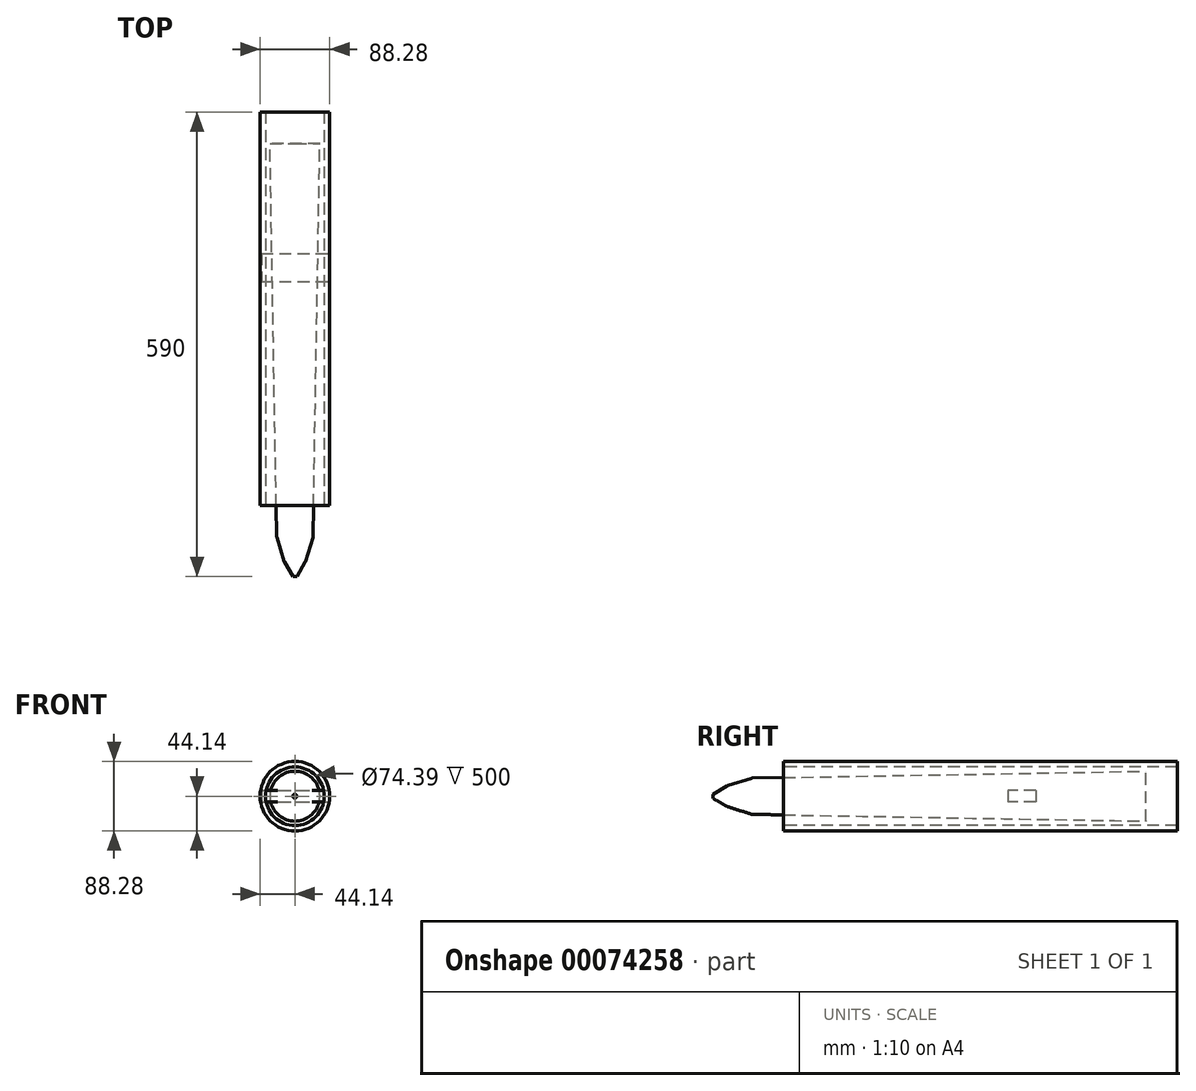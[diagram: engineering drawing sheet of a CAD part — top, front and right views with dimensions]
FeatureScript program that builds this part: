
annotation { "Feature Type Name" : "Feature", "Feature Type Description" : "" }
export const myFeature = defineFeature(function(context is Context, id is Id, definition is map)
    precondition{}
    {
        {
            var Q0;
            Q0=qCreatedBy(makeId("Front.planeOp"),FACE);
            var sketch = newSketch(context, id + "F0", { "sketchPlane" : qUnion([Q0])});
            skCircle(sketch, "E0", {"center": v(0, 0) * mm, "radius": 44.14 * mm});
            skSolve(sketch);
        }
        {
            var Q0;
            Q0=makeQuery(id+"F0.imprint","IMPRINT",FACE,{"disambiguationData":[TD([[makeQuery(id+"F0.imprint","IMPRINT",EDGE,{"derivedFrom":sQuery(id+"F0.wireOp",EDGE,"E0")}),1.0]])]});
            extrude(context, id + "F1", {"entities" : qUnion([Q0]), "endBound" : BoundingType.SYMMETRIC, "depth" : 500 * mm});
        }
        {
            var Q0;
            Q0=qCreatedBy(makeId("Front.planeOp"),FACE);
            var sketch = newSketch(context, id + "F2", { "sketchPlane" : qUnion([Q0])});
            skCircle(sketch, "E1", {"center": v(0, 0) * mm, "radius": 37.2 * mm});
            skSolve(sketch);
        }
        {
            var Q0;
            Q0=makeQuery(id+"F2.imprint","IMPRINT",FACE,{"disambiguationData":[TD([[makeQuery(id+"F2.imprint","IMPRINT",EDGE,{"derivedFrom":sQuery(id+"F2.wireOp",EDGE,"E1")}),1.0]])]});
            extrude(context, id + "F3", {"entities" : qUnion([Q0]), "operationType" : NewBodyOperationType.REMOVE, "endBound" : BoundingType.SYMMETRIC, "oppositeDirection" : true, "depth" : 550 * mm});
        }
        {
            var Q0;
            Q0=qCreatedBy(makeId("Front.planeOp"),FACE);
            cPlane(context, id + "F4", {"entities" : qUnion([Q0]), "cplaneType" : CPlaneType.OFFSET, "offset" : 290 * mm, "width" : 150 * mm, "height" : 150 * mm});
        }
        {
            var Q0;
            Q0=qCreatedBy(id+"F4.planeOp",FACE);
            var sketch = newSketch(context, id + "F5", { "sketchPlane" : qUnion([Q0])});
            skCircle(sketch, "E2", {"center": v(0, 0) * mm, "radius": 23.03 * mm});
            skSolve(sketch);
        }
        {
            var Q0;
            Q0=qCreatedBy(id+"F4.planeOp",FACE);
            cPlane(context, id + "F6", {"entities" : qUnion([Q0]), "cplaneType" : CPlaneType.OFFSET, "offset" : 500 * mm, "oppositeDirection" : true, "width" : 150 * mm, "height" : 150 * mm});
        }
        {
            var Q0;
            Q0=qCreatedBy(id+"F6.planeOp",FACE);
            var sketch = newSketch(context, id + "F7", { "sketchPlane" : qUnion([Q0])});
            skCircle(sketch, "E3", {"center": v(0, 0) * mm, "radius": 31.73 * mm});
            skSolve(sketch);
        }
        {
            var Q1;
            Q1 = qSketchRegion(id + "F7", true);
            var Q2;
            Q2 = qSketchRegion(id + "F5", true);
            loft(context, id + "F8", {"operationType" : NewBodyOperationType.ADD, "sheetProfilesArray" : [{ "sheetProfileEntities" : qUnion([Q1]) }, { "sheetProfileEntities" : qUnion([Q2]) }]});
        }
        {
            var Q0;
            Q0=qCreatedBy(makeId("Top.planeOp"),FACE);
            var sketch = newSketch(context, id + "F9", { "sketchPlane" : qUnion([Q0])});
            skLineSegment(sketch, "E4", {"start": v(0, 70.47) * mm, "end": v(-42.54, 70.47) * mm});
            skLineSegment(sketch, "E5", {"start": v(-42.54, 70.47) * mm, "end": v(-42.54, 34.9) * mm});
            skLineSegment(sketch, "E6", {"start": v(-42.54, 34.9) * mm, "end": v(0, 34.9) * mm});
            skLineSegment(sketch, "E7.MirrorCS", {"start": v(0, 70.47) * mm, "end": v(42.54, 70.47) * mm});
            skLineSegment(sketch, "E8.MirrorCS", {"start": v(42.54, 70.47) * mm, "end": v(42.54, 34.9) * mm});
            skLineSegment(sketch, "E9.MirrorCS", {"start": v(42.54, 34.9) * mm, "end": v(0, 34.9) * mm});
            skSolve(sketch);
        }
        {
            var Q0;
            Q0 = qSketchRegion(id + "F9", true);
            extrude(context, id + "F10", {"entities" : qUnion([Q0]), "endBound" : BoundingType.SYMMETRIC, "depth" : 15 * mm});
        }
        {
            var Q0;
            Q0=qCreatedBy(id+"F4.planeOp",FACE);
            cPlane(context, id + "F11", {"entities" : qUnion([Q0]), "cplaneType" : CPlaneType.OFFSET, "offset" : 50 * mm, "width" : 150 * mm, "height" : 150 * mm});
        }
        {
            var Q0;
            Q0=qCreatedBy(id+"F11.planeOp",FACE);
            var sketch = newSketch(context, id + "F12", { "sketchPlane" : qUnion([Q0])});
            skCircle(sketch, "E10", {"center": v(0, 0) * mm, "radius": 7.6 * mm});
            skSolve(sketch);
        }
        {
            var Q1;
            Q1=makeQuery(id+"F8.opLoft","CAP_FACE",FACE,{"disambiguationData":[OSD([makeQuery(id+"F5.imprint","IMPRINT",FACE,{"disambiguationData":[TD([[makeQuery(id+"F5.imprint","IMPRINT",EDGE,{"derivedFrom":sQuery(id+"F5.wireOp",EDGE,"E2")}),1.0]])]})])],"isStart":true});
            var Q2;
            Q2=makeQuery(id+"F12.imprint","IMPRINT",FACE,{"disambiguationData":[TD([[makeQuery(id+"F12.imprint","IMPRINT",EDGE,{"derivedFrom":sQuery(id+"F12.wireOp",EDGE,"E10")}),1.0]])]});
            loft(context, id + "F13", {"operationType" : NewBodyOperationType.ADD, "sheetProfilesArray" : [{ "sheetProfileEntities" : qUnion([Q1]) }, { "sheetProfileEntities" : qUnion([Q2]) }]});
        }
        {
            var Q0;
            Q0=makeQuery(id+"F13.opLoft","MID_CAP_EDGE",EDGE,{"disambiguationData":[OSD([sQuery(id+"F5.wireOp",EDGE,"E2"),sQuery(id+"F7.wireOp",EDGE,"E3"),sQuery(id+"F12.wireOp",EDGE,"E10")])],"capPos":1.0});
            chamfer(context, id + "F14", {"entities" : qUnion([Q0]), "chamferType" : ChamferType.OFFSET_ANGLE, "width" : 5 * mm, "oppositeDirection" : false, "angle" : 60 * degree, "tangentPropagation" : true});
        }
        {
            var Q0;
            {var subQ0=sQuery(id+"F12.wireOp",EDGE,"E10");var subQ1=sQuery(id+"F7.wireOp",EDGE,"E3");var subQ2=sQuery(id+"F5.wireOp",EDGE,"E2");Q0=makeQuery(id+"F14.opChamfer","BLEND_EDGE",EDGE,{"blendedFrom":[makeQuery(id+"F13.opLoft","MID_CAP_EDGE",EDGE,{"disambiguationData":[OSD([subQ2,subQ1,subQ0])],"capPos":1.0}),makeQuery(id+"F13.opLoft","SWEPT_FACE",FACE,{"disambiguationData":[OSD([subQ2,subQ1,subQ0])]})],"blendedInto":[makeQuery(id+"F13.opLoft","SWEPT_FACE",FACE,{"disambiguationData":[OSD([subQ2,subQ1,subQ0])]})]});}
            var Q1;
            {var subQ0=sQuery(id+"F7.wireOp",EDGE,"E3");var subQ1=sQuery(id+"F5.wireOp",EDGE,"E2");Q1=makeQuery(id+"F13.boolean.opBoolean","MERGE",EDGE,{"derivedFrom":[makeQuery(id+"F8.opLoft","MID_CAP_EDGE",EDGE,{"disambiguationData":[OSD([subQ1,subQ0])],"capPos":1.0}),makeQuery(id+"F13.opLoft","MID_CAP_EDGE",EDGE,{"disambiguationData":[OSD([subQ1,subQ0])],"capPos":0.0})]});}
            fillet(context, id + "F15", {"entities" : qUnion([Q0, Q1]), "radius" : 5 * mm, "tangentPropagation" : true, "allowEdgeOverflow" : false});
        }
    });
